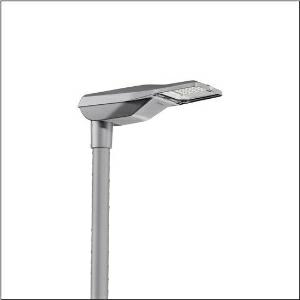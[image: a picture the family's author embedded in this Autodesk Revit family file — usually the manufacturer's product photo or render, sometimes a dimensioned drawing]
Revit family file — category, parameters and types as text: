
# Revit family: streetlight_sl_21_iq_micro___st1_5a_5xe1p31d08db_ec34
name_source: partatom
category: Lighting Fixtures
units: mm (PartAtom-declared; Revit-internal decimal feet)

## family parameters
Cut with Voids When Loaded = No
Host = Face
Light Source = No
Part Type = Normal
Room Calculation Point = No
Round Connector Dimension = Use Diameter
Shared = No

## types (1)
- --- (1 x LED, 4730 lm, 36.4 W, 3000K)
    Apparent Load = 36 VA
    CIE Flux Codes = 22 53 95 100 100
    Color Rendering = 70
    Color Temperature = 3000K
    Default Elevation = 1800 mm
    Description = Streetlight SL 21 iQ micro, mast luminaire, primary light control with lens, of PMMA, primary optical cover: cover, of toughened safety glass, transparent, light distribution: ST1.5a, light emission: direct distribution, primary light characteristic: asymmetric, installation type: post-top, side-entry, LED, High Power LED, rated luminous flux: 4.730lm, luminous efficacy: 130lm/W, light colour: 730, colour temperature: 3000K, control gear: iQ-Comfort, control: Auto-Match, Temp-Guard, Lumen-Switch, Night-Set, Smart-Wire, Light-Fading, Desk-Remote (wireless, voltage-free reading and setting of iQ features in the workshop via application-optimized NFC function/RFID function), optimised constant luminous flux control (CLO 2.0), pre-setting: linear dimming characteristic, mains connection: 220..240V, AC, 50/60Hz, start of lifetime: 36W, end of service life: 38W, reduction: 16W, luminaire housing, of diecast aluminium, powder-coated, Siteco® metallic grey (DB 702S), corrosivity category C5 mid according to DIN EN ISO 12944, please order mast flange separately, inclination adjustable: 0°, 5°, 10°, 15°, sealing non-destructively replaceable, multi-level sealing system, length: 528mm, width: 235mm, height: 110mm, mast flange for spigot size: 42mm (side-entry): 5XC10008XM4, 60/48mm (side-entry/post-top): 5XC10108XM2, 76/60mm (side-entry/post-top): 5XC10108XM1, protection rating (complete): IP66, insulation class (complete): insulation class II (safety insulation), certification: CE, ENEC, ENEC+, VDE, impact resistance: IK10, permissible operating ambient temperature for outdoor applications: -40..+50°C, standard-compliant lighting for roads and squares, packaging unit: 1 piece

Light Distribution: ST1.5a
    Height = 110 mm
    Lamp = 1 x LED
    Lamp Light Flux = 4730 lm
    Lamp Power = 36.4 W
    Lamp count = 1
    Length = 528 mm
    Luminous efficacy = 130 lm/W
    Manufacturer = Siteco
    ModVariant = No
    Model = 5XE1P31D08DB
    Number of Poles = 1
    OnlyDefault = Yes
    Power Factor = 1
    Product Name = Streetlight SL 21 iQ micro | ST1.5a
    Product group = mast luminaire | pylon top
    ProductGroupID = 6100
    Protection Class = Protection class II
    Protection Degree = IP 66
    RLX_Detail_Level = 1
    RLX_Emergency_Light_Flux = 0 lm
    RLX_Emergency_Type = 0
    RLX_Emergency_Type_DB = No
    RlxData = <blob elided: 102917 chars, md5=3efe38d2>
    Socket = socket
    Standby Power = 0 W
    System Light Flux = 4730 lm
    System Power = 36 W
    Type Comments = factory setting: luminous flux: 100 % | dim-lin: 254 | 715 mA
    Type Image = l_1006881.jpg
    URL = http://relux.com
    VarID = @adj_175381
    Voltage = 0 V
    Weight = 0.00 kg
    Width = 235 mm

## geometry (parser evidence)
native form markers: Blend x4, Sweep x11
no freeform markers — native parametric forms only
